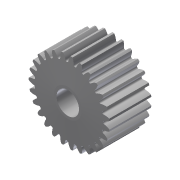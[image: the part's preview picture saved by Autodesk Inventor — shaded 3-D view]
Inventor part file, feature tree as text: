
AUTODESK INVENTOR PART (.ipt)
format: ipt  version: 2013 (Build 170138000, 138)  size: 402,944 bytes
history: native  units: in
note: dims shown in document units (in); Inventor stores cm internally (conversion verified against a paired STEP export)
features: mirror x1, other x1, imported_body x1
ambient origin geometry x8: Origin, YZ Plane, XZ Plane, XY Plane, X Axis, Y Axis, Z Axis, Center Point
feature tree (3):
  mirror  "Mirror2"
  other  "217-2726-003 Rev1_27t Planet1"
  imported_body  "Base1"
